# Revit family: WCPan-54cm-WallHung-Vitra_MemoriaSeries_5885
name_source: partatom
category: Plumbing Fixtures
revit_build: Autodesk Revit 2017 (Build: 20160225_1515(x64)
units: mm (PartAtom-declared; Revit-internal decimal feet)

## family parameters
Cut with Voids When Loaded = No
Host = Face
OmniClass Number = 23.45.05.21.11
OmniClass Title = Water Closets
Part Type = Normal
Room Calculation Point = No
Round Connector Dimension = Use Diameter
Shared = Yes

## types (16) — shared parameters
BIMobject category = Sanitary - Toilets
Brand = VitrA
CW Connection = Yes
Default Elevation = 410 mm
Description = VitrA Memoria Rim-ex Wall-hung WC pan
Design country = Turkey
HW Connection = No
IFC Classification = Sanitary Terminal
Main Material = Ceramic
Manufacturer = VitrA
Manufacturer name = Vitra
Masterformat 2014 Code = 22 45 26
Masterformat 2014 Description = Sanitary Facilities
Mounting type = Wall Hung
NBS Referans Code = 35-65-90
NBS Referans Description = Toilet Systems
Nominal Depth (mm) = 545 mm  [stored 1.78806 ft]
Nominal Height (mm) = 350 mm  [stored 1.14829 ft]
Nominal Width (mm) = 430 mm  [stored 1.41076 ft]
OmniClass Code = 23-31 19 00
OmniClass Description = Toilets
Primary Material = <By Category>
Product certification = https://www.vitraglobal.com
Product family = Memoria
UNSPSC Code = 301815
UNSPSC Description = Sanitary Ware
URL = https://www.vitraglobal.com
Uniclass 1.4 Code = L7216
Uniclass 1.4 Description = Toilets
Uniclass 2.0 Code = SS-35-65-90
Uniclass 2.0 Description = Toilet Systems
Uniclass 2015 Code = Pr_40_20_93
Uniclass 2015 Name = Urinal and WC fittings
Uniformat II Code = D2010
Uniformat II Description = Sanitary Facilities
Vent Connection = No
Warranty Period (Year) = 10 Years
Waste Connection = Yes
Weight Net (kg) = 29.320
Youtube = https://www.youtube.com

## per-type parameters (varying)
| type | Article No. (default) | Color | Installation instructions | Model | Product Guid | Product SKU | Product data url | Product group | Product url | Secondary Material | Technical description | With Bidet Function |
| WC_WallHung_Vitra_Memoria(MatteBlack)_5885B483-0101 | 5885B483-0101 | MatteBlack | https://cdn.vitra.com.tr | 5885B483-0101 | https://cdn.vitra.com.tr | 5885B483-0101 | https://www.vitraglobal.com | WallHung WC |  | Black | https://www.vitraglobal.com | No |
| WC_WallHung_Vitra_Memoria(MatteBeige)_5885B420-0101 | 5885B420-0101 | MatteBeige | https://cdn.vitra.com.tr | 5885B420-0101 | https://cdn.vitra.com.tr | 5885B420-0101 | https://www.vitraglobal.com | WallHung WC |  | Beige | https://www.vitraglobal.com | No |
| WC_WallHung_Vitra_Memoria(MatteWhite)_5885B401-0101 | 5885B401-0101 | MatteWhite | https://cdn.vitra.com.tr | 5885B401-0101 | https://cdn.vitra.com.tr | 5885B401-0101 | https://www.vitraglobal.com | WallHung WC |  | MatteWhite | https://www.vitraglobal.com | No |
| WC_WallHung_Vitra_Memoria(White)_5885B403-0101 | 5885B403-0101 | White | https://cdn.vitra.com.tr | 5885B403-0101 | https://cdn.vitra.com.tr | 5885B403-0101 | https://www.bimobject.com | Wall Hung WC | https://www.vitraglobal.com | White | https://www.vitraglobal.com | No |
| WC_WallHung_Vitra_Memoria(White)_5885B403-0559 | 5885B403-0559 | White |  | 5885B403-0559 |  | 5885B403-0559 | https://www.bimobject.com | Wall Hung WC | https://www.vitra.com.tr | White | https://www.vitra.com.tr | Yes |
| WC_WallHung_Vitra_Memoria(MatteWhite)_5885B401-0559 | 5885B401-0559 | MatteWhite |  | 5885B401-0559 |  | 5885B401-0559 |  | WallHung WC | https://www.vitra.com.tr | MatteWhite | https://www.vitra.com.tr | Yes |
| WC_WallHung_Vitra_Memoria(MatteBeige)_5885B420-0559 | 5885B420-0559 | MatteBeige |  | 5885B420-0559 |  | 5885B420-0559 |  | WallHung WC | https://www.vitra.com.tr | Beige | https://www.vitra.com.tr | Yes |
| WC_WallHung_Vitra_Memoria(MatteBlack)_5885B483-0559 | 5885B483-0559 | MatteBlack |  | 5885B483-0559 |  | 5885B483-0559 |  | WallHung WC | https://www.vitra.com.tr | Black | https://www.vitra.com.tr | Yes |
| WC_WallHung_Vitra_Memoria(White)_5885B403H0101 | 5885B403H0101 | White |  | 5885B403H0101 |  | 5885B403H0101 |  | Wall Hung WC | https://www.vitra-india.com | White | https://www.vitra-india.com | No |
| WC_WallHung_Vitra_Memoria(White)_5885B403H0559 | 5885B403H0559 | White |  | 5885B403H0559 |  | 5885B403H0559 |  | Wall Hung WC | https://www.vitra-india.com | White | https://www.vitra-india.com | Yes |
| WC_WallHung_Vitra_Memoria(MatteWhite)_5885B401H0101 | 5885B401H0101 | MatteWhite |  | 5885B401H0101 |  | 5885B401H0101 |  | WallHung WC | https://www.vitra-india.com | MatteWhite | https://www.vitra-india.com | No |
| WC_WallHung_Vitra_Memoria(MatteWhite)_5885B401H0559 | 5885B401H0559 | MatteWhite |  | 5885B401H0559 |  | 5885B401H0559 |  | WallHung WC | https://www.vitra-india.com | MatteWhite | https://www.vitra-india.com | Yes |
| WC_WallHung_Vitra_Memoria(MatteBeige)_5885B420H0101 | 5885B420H0101 | MatteBeige |  | 5885B420H0101 |  | 5885B420H0101 |  | WallHung WC | https://www.vitra-india.com | Beige | https://www.vitra-india.com | No |
| WC_WallHung_Vitra_Memoria(MatteBeige)_5885B420H0559 | 5885B420H0559 | MatteBeige |  | 5885B420H0559 |  | 5885B420H0559 |  | WallHung WC | https://www.vitra-india.com | Beige | https://www.vitra-india.com | Yes |
| WC_WallHung_Vitra_Memoria(MatteBlack)_5885B483H0101 | 5885B483H0101 | MatteBlack |  | 5885B483H0101 |  | 5885B483H0101 |  | WallHung WC | https://www.vitra-india.com | Black | https://www.vitra-india.com | No |
| WC_WallHung_Vitra_Memoria(MatteBlack)_5885B483H0559 | 5885B483H0559 | MatteBlack |  | 5885B483H0559 |  | 5885B483H0559 |  | WallHung WC | https://www.vitra-india.com | Black | https://www.vitra-india.com | Yes |

note: [stored X ft] marks values corroborated as IEEE doubles in the binary element streams (Revit-internal decimal feet)

## geometry (parser evidence)
native form markers: Sweep x3
no freeform markers — native parametric forms only
